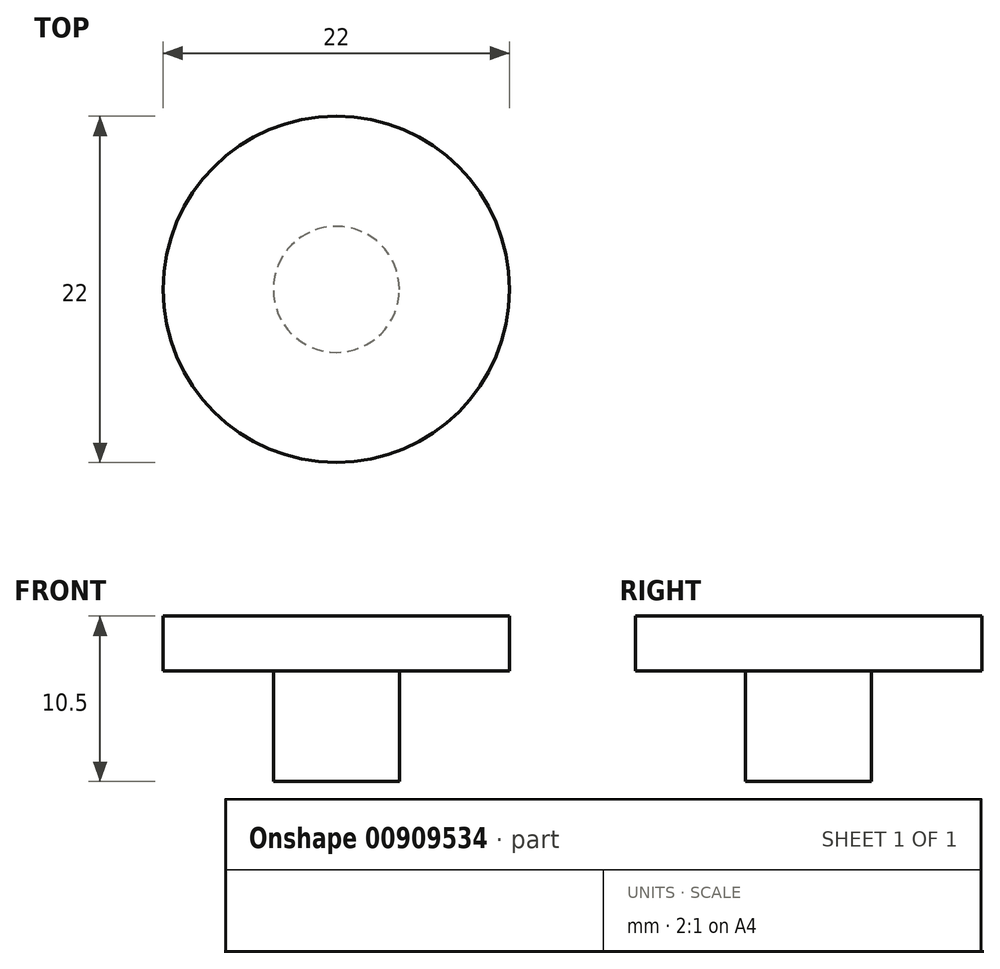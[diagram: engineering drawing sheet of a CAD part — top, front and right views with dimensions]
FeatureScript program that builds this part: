
annotation { "Feature Type Name" : "Feature", "Feature Type Description" : "" }
export const myFeature = defineFeature(function(context is Context, id is Id, definition is map)
    precondition{}
    {
        {
            var Q0;
            Q0=qCreatedBy(makeId("Front.planeOp"),FACE);
            var sketch = newSketch(context, id + "F0", { "sketchPlane" : qUnion([Q0])});
            skLineSegment(sketch, "E0.bottom", {"start": v(-4, 7) * mm, "end": v(0, 7) * mm});
            skLineSegment(sketch, "E0.top", {"start": v(-4, 0) * mm, "end": v(0, 0) * mm});
            skLineSegment(sketch, "E0.left", {"start": v(-4, 7) * mm, "end": v(-4, 0) * mm});
            skLineSegment(sketch, "E0.right", {"start": v(0, 7) * mm, "end": v(0, 0) * mm});
            skLineSegment(sketch, "E1.bottom", {"start": v(-11, 10.5) * mm, "end": v(0, 10.5) * mm});
            skLineSegment(sketch, "E1.top", {"start": v(-11, 7) * mm, "end": v(0, 7) * mm});
            skLineSegment(sketch, "E1.left", {"start": v(-11, 10.5) * mm, "end": v(-11, 7) * mm});
            skLineSegment(sketch, "E1.right", {"start": v(0, 10.5) * mm, "end": v(0, 7) * mm});
            skSolve(sketch);
        }
        {
            var Q0;
            Q0=makeQuery(id+"F0.imprint","IMPRINT",FACE,{"disambiguationData":[TD([[makeQuery(id+"F0.imprint","IMPRINT",EDGE,{"derivedFrom":sQuery(id+"F0.wireOp",EDGE,"E0.bottom")}),1.0]])]});
            var Q1;
            Q1=makeQuery(id+"F0.imprint","IMPRINT",FACE,{"disambiguationData":[TD([[makeQuery(id+"F0.imprint","IMPRINT",EDGE,{"derivedFrom":sQuery(id+"F0.wireOp",EDGE,"E0.bottom")}),-1.0]])]});
            var Q2;
            Q2=sQuery(id+"F0.wireOp",EDGE,"E1.right");
            revolve(context, id + "F1", {"surfaceOperationType" : NewSurfaceOperationType.NEW, "entities" : qUnion([Q0, Q1]), "axis" : qUnion([Q2]), "revolveType" : RevolveType.FULL});
        }
    });
